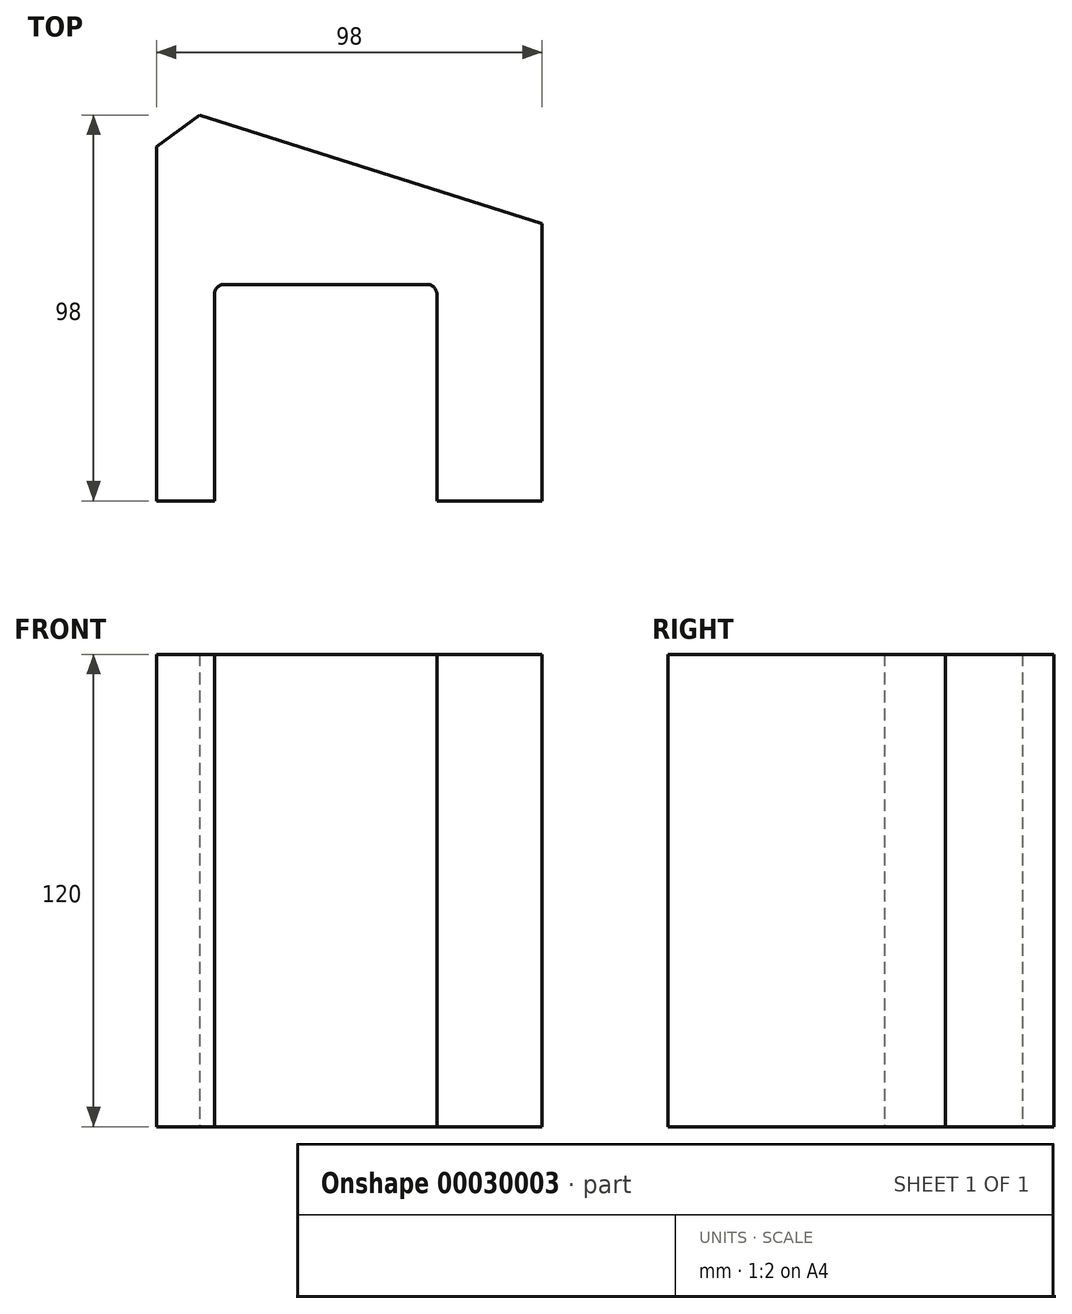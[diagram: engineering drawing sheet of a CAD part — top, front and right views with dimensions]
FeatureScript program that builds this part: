
annotation { "Feature Type Name" : "Feature", "Feature Type Description" : "" }
export const myFeature = defineFeature(function(context is Context, id is Id, definition is map)
    precondition{}
    {
        {
            var Q0;
            Q0=qCreatedBy(makeId("Top.planeOp"),FACE);
            var sketch = newSketch(context, id + "F0", { "sketchPlane" : qUnion([Q0])});
            skLineSegment(sketch, "E0", {"start": v(0, 0) * mm, "end": v(14.75, 0) * mm});
            skLineSegment(sketch, "E1", {"start": v(14.75, 0) * mm, "end": v(14.75, 52.5) * mm});
            skLineSegment(sketch, "E2", {"start": v(17.25, 55) * mm, "end": v(68.75, 55) * mm});
            skLineSegment(sketch, "E3", {"start": v(71.25, 52.5) * mm, "end": v(71.25, 0) * mm});
            skLineSegment(sketch, "E4", {"start": v(71.25, 0) * mm, "end": v(98, 0) * mm});
            skLineSegment(sketch, "E5", {"start": v(98, 0) * mm, "end": v(98, 70.4) * mm});
            skLineSegment(sketch, "E6", {"start": v(98, 70.4) * mm, "end": v(10.9, 98) * mm});
            skLineSegment(sketch, "E7", {"start": v(10.9, 98) * mm, "end": v(0, 90) * mm});
            skLineSegment(sketch, "E8", {"start": v(0, 90) * mm, "end": v(0, 0) * mm});
            skPoint(sketch, "E9.visualSharp", {"position": v(14.75, 55) * mm});
            skArc(sketch, "E9.filletArc", {"start": v(17.25, 55) * mm, "mid": v(15.48, 54.27) * mm, "end": v(14.75, 52.5) * mm});
            skPoint(sketch, "E10.visualSharp", {"position": v(71.25, 55) * mm});
            skArc(sketch, "E10.filletArc", {"start": v(71.25, 52.5) * mm, "mid": v(70.52, 54.27) * mm, "end": v(68.75, 55) * mm});
            skSolve(sketch);
        }
        {
            var Q0;
            Q0 = qSketchRegion(id + "F0", true);
            extrude(context, id + "F1", {"entities" : qUnion([Q0]), "depth" : 120 * mm});
        }
    });
